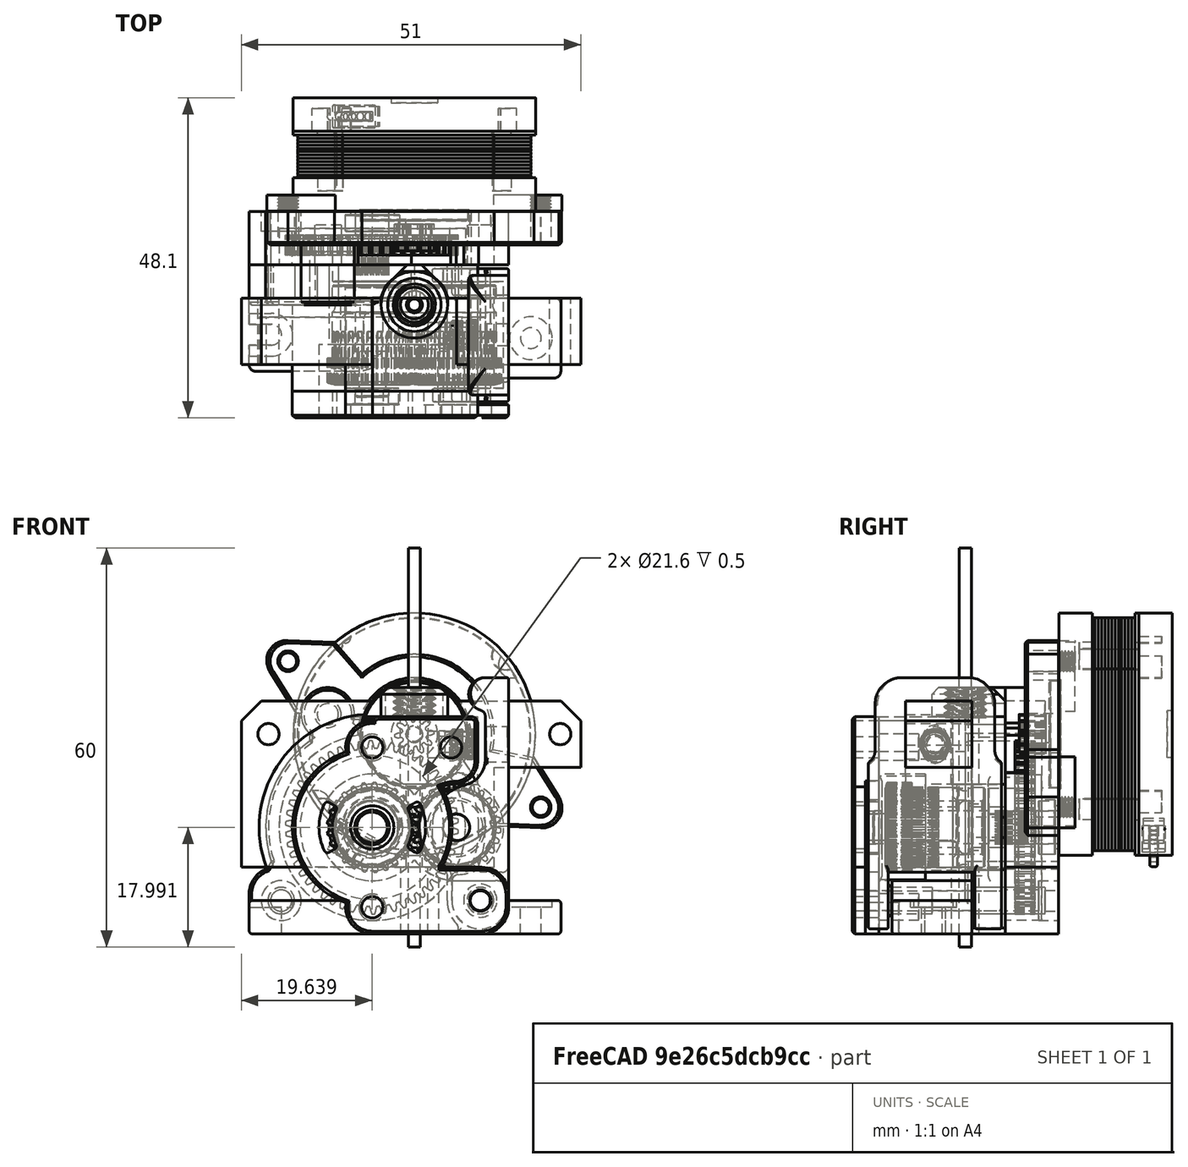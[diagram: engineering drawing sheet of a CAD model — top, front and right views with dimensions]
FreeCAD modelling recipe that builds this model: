
FCSTD DOCUMENT  (FreeCAD 0.18R16146 (Git))
Label: main-1
License: All rights reserved
LicenseURL: http://en.wikipedia.org/wiki/All_rights_reserved
objects: Part::Cylinder×61, Part::Cut×40, Part::MultiFuse×25, Part::Feature×21, Part::Box×20, Part::Fillet×20, Part::Chamfer×19, Part::MultiCommon×2
note: 208 computed .brp shape members not serialized (recipe doc carries the construction recipe); baked Part::Feature solids carry a one-line shape summary decoded from their .brp

FEATURE [Part::Feature] Part__Feature072  label="FlyGear"
  Placement = pos=(6.30321,-3.05009,17.9985) rot=(0,1,0;1.57818rad)
  shape: bbox 15.15 x 20 x 15.15 mm, 372 faces (baked)
FEATURE [Part::Feature] Part__Feature004  label="LatchShaft"
  Placement = pos=(9.90321,14.3499,6.99894) rot=(0.999993,0.00265,-0.00265;1.5708rad)
  shape: bbox 3.247 x 20 x 3.247 mm, 5 faces (baked)
FEATURE [Part::Feature] Part__Feature028  label="insert M3 v1"
  Placement = pos=(3.65321,4.45,30.4999) rot=(-0.57735,-0.57735,-0.57735;2.0944rad)
  shape: bbox 5.909 x 4.726 x 4.72 mm, 153 faces (baked)
FEATURE [Part::Feature] Part__Feature006  label="T10 SpurGear"
  Placement = pos=(3.9913e-08,-1.44113e-07,9e-15) rot=(0,0,1;0.017453rad)
  shape: bbox 6 x 5.817 x 5.76 mm, 83 faces (baked)
FEATURE [Part::Feature] Fusion001002002001003  label="name14"
  shape: bbox 50.3 x 39.95 x 23 mm, 596 faces (baked)
FEATURE [Part::MultiFuse] Fusion  label="moto-with-gear"
  Placement = pos=(0,17.1,32) rot=(-0.935113,0.250563,0.250563;1.63783rad)
  Shapes = -> [Part__Feature006,Fusion001002002001003]
FEATURE [Part::Feature] Fusion001  label="motor-cut"
  Placement = pos=(0,7e-15,32) rot=(-1,0,0;1.5708rad)
  shape: bbox 47.04 x 10 x 16.2 mm, 9 faces, 3 solids (baked)
FEATURE [Part::Box] Box  label="Cube"
  AttacherType = Attacher::AttachEngine3D
  Height = 25
  Length = 51
  Placement = pos=(-26,0,12) rot=(0,0,1;0rad)
  Width = 10
FEATURE [Part::Cylinder] Cylinder
  Angle = 360
  AttacherType = Attacher::AttachEngine3D
  Height = 10
  Placement = pos=(-6.325,-2.85,18) rot=(-1,0,0;1.5708rad)
  Radius = 17
FEATURE [Part::Cylinder] Cylinder001
  Angle = 360
  AttacherType = Attacher::AttachEngine3D
  Height = 10
  Placement = pos=(-6.325,8e-15,18) rot=(-1,0,0;1.5708rad)
  Radius = 3.25
FEATURE [Part::Cylinder] Cylinder002
  Angle = 360
  AttacherType = Attacher::AttachEngine3D
  Height = 10
  Placement = pos=(-6.325,-0.45,18) rot=(-1,0,0;1.5708rad)
  Radius = 4.1
FEATURE [Part::Cut] Cut
  Base = -> Box
  Tool = -> Cylinder
FEATURE [Part::Cut] Cut001
  Base = -> Cut
  Tool = -> Cylinder002
FEATURE [Part::Cut] Cut002
  Base = -> Cut001
  Tool = -> Cylinder001
FEATURE [Part::Chamfer] Chamfer
  Base = -> Cut002
  Edges = 1 edges r=0.5: [Edge25]
FEATURE [Part::Chamfer] Chamfer001
  Base = -> Chamfer
  Edges = 2 edges r=3: [Edge26,Edge27]
FEATURE [Part::Box] Box001  label="Cube001"
  AttacherType = Attacher::AttachEngine3D
  Height = 15
  Length = 14
  Placement = pos=(12,0,12) rot=(0,0,1;0rad)
  Width = 10
FEATURE [Part::Cut] Cut003
  Base = -> Chamfer001
  Tool = -> Box001
FEATURE [Part::Cut] Cut004  label="320-aligner-test"
  Base = -> Cut003
  Tool = -> Fusion001
FEATURE [Part::Feature] Common001001  label="back-plate-base"
  Placement = pos=(0,15,32) rot=(-0.935113,0.250563,0.250563;1.63783rad)
  shape: bbox 44.17 x 8 x 36 mm, 14 faces (baked)
FEATURE [Part::Cylinder] Cylinder003
  Angle = 360
  AttacherType = Attacher::AttachEngine3D
  Height = 8
  Placement = pos=(-6.325,23,18) rot=(1,0,0;1.5708rad)
  Radius = 16
FEATURE [Part::Feature] Part__Feature056001001002001  label="bearing002"
  shape: bbox 8 x 2.5 x 8 mm, 12 faces (baked)
FEATURE [Part::Feature] Fusion001001001  label="asembly-shaft001"
  Placement = pos=(0.2,0,0) rot=(0,0,1;0rad)
  shape: bbox 25.99 x 28 x 26 mm, 508 faces (baked)
FEATURE [Part::Feature] Part__Feature056001001001001  label="bearing003"
  Placement = pos=(0.2,0,0) rot=(0,0,1;0rad)
  shape: bbox 8 x 2.5 x 8 mm, 12 faces (baked)
FEATURE [Part::Feature] Part__Feature071001  label="MotorGear001"
  Placement = pos=(0.2,0,0) rot=(0,0,1;0rad)
  shape: bbox 14.64 x 15 x 14.64 mm, 359 faces (baked)
FEATURE [Part::Cylinder] Cylinder004
  Angle = 360
  AttacherType = Attacher::AttachEngine3D
  Height = 7
  Placement = pos=(-6.325,20.5,18) rot=(1,0,0;1.5708rad)
  Radius = 14
FEATURE [Part::Cylinder] Cylinder006
  Angle = 360
  AttacherType = Attacher::AttachEngine3D
  Height = 10
  Placement = pos=(-6.325,23,18) rot=(1,0,0;1.5708rad)
  Radius = 3.25
FEATURE [Part::Cylinder] Cylinder007
  Angle = 360
  AttacherType = Attacher::AttachEngine3D
  Height = 10
  Placement = pos=(-6.325,22.5,18) rot=(1,0,0;1.5708rad)
  Radius = 4.1
FEATURE [Part::Cylinder] Cylinder010  label="filament"
  Angle = 360
  AttacherType = Attacher::AttachEngine3D
  Height = 60
  Placement = pos=(0,9,0) rot=(0,0,1;0rad)
  Radius = 0.9
FEATURE [Part::Cylinder] Cylinder011
  Angle = 360
  AttacherType = Attacher::AttachEngine3D
  Height = 10
  Placement = pos=(0,18,32) rot=(1,0,0;1.5708rad)
  Radius = 27.1
FEATURE [Part::Cylinder] Cylinder012
  Angle = 142
  AttacherType = Attacher::AttachEngine3D
  Height = 10
  Placement = pos=(0,23,32) rot=(0.990855,0.095409,-0.095409;1.57998rad)
  Radius = 26
FEATURE [Part::Cylinder] Cylinder013
  Angle = 360
  AttacherType = Attacher::AttachEngine3D
  Height = 10
  Placement = pos=(0,23,32) rot=(1,0,0;1.5708rad)
  Radius = 12
FEATURE [Part::Feature] Fusion001002002001004  label="motor-cut001"
  Placement = pos=(0,23,32) rot=(0.935113,0.250563,-0.250563;1.63783rad)
  shape: bbox 41.07 x 10 x 25.02 mm, 9 faces, 3 solids (baked)
FEATURE [Part::Cut] Cut006
  Base = -> Cylinder012
  Tool = -> Cylinder013
FEATURE [Part::Cylinder] Cylinder014
  Angle = 360
  AttacherType = Attacher::AttachEngine3D
  Height = 10
  Placement = pos=(0,23,32) rot=(1,0,0;1.5708rad)
  Radius = 8.5
FEATURE [Part::Feature] Part__Feature  label="Latch"
  Placement = pos=(-6.34679,-10.5501,18) rot=(1,0,0;3.14159rad)
  shape: bbox 20.03 x 24 x 38.43 mm, 141 faces (baked)
FEATURE [Part::Cylinder] Cylinder015
  Angle = 360
  AttacherType = Attacher::AttachEngine3D
  Height = 10
  Placement = pos=(-6.325,22,18) rot=(1,0,0;1.5708rad)
  Radius = 15
FEATURE [Part::Chamfer] Chamfer008
  Base = -> Cylinder015
  Edges = 1 edges r=1: [Edge3]
FEATURE [Part::Box] Box002  label="Cube002"
  AttacherType = Attacher::AttachEngine3D
  Height = 10
  Length = 20.5
  Placement = pos=(-6.325,15,2) rot=(0,0,1;0rad)
  Width = 8
FEATURE [Part::Fillet] Fillet
  Base = -> Box002
  Edges = 1 edges r=5: [Edge8]
FEATURE [Part::Fillet] Fillet001
  Base = -> Fillet
  Edges = 1 edges r=4: [Edge3]
FEATURE [Part::Cylinder] Cylinder016
  Angle = 360
  AttacherType = Attacher::AttachEngine3D
  Height = 10
  Placement = pos=(9.925,21,7) rot=(1,0,0;1.5708rad)
  Radius = 2
FEATURE [Part::Box] Box003  label="Cube003"
  AttacherType = Attacher::AttachEngine3D
  Height = 10
  Length = 18.5
  Placement = pos=(-24.83,15,2) rot=(0,0,1;0rad)
  Width = 8
FEATURE [Part::Cylinder] Cylinder018  label="Cylinder017"
  Angle = 360
  AttacherType = Attacher::AttachEngine3D
  Height = 11
  Placement = pos=(-20,25,7) rot=(1,0,0;1.5708rad)
  Radius = 1.6
FEATURE [Part::Feature] Chamfer008001  label="Chamfer011"
  shape: bbox 30 x 10 x 30 mm, 4 faces (baked)
FEATURE [Part::Cylinder] Cylinder019  label="Cylinder018"
  Angle = 360
  AttacherType = Attacher::AttachEngine3D
  Height = 8
  Placement = pos=(-13,23,35) rot=(1,0,0;1.5708rad)
  Radius = 4
FEATURE [Part::Cylinder] Cylinder020  label="Cylinder019"
  Angle = 360
  AttacherType = Attacher::AttachEngine3D
  Height = 8
  Placement = pos=(-13,21,35) rot=(1,0,0;1.5708rad)
  Radius = 2
FEATURE [Part::Cut] Cut016
  Base = -> Common001001
  Tool = -> Cylinder011
FEATURE [Part::Cut] Cut017
  Base = -> Cut016
  Tool = -> Cut006
FEATURE [Part::Cut] Cut018
  Base = -> Cut017
  Tool = -> Fusion001002002001004
FEATURE [Part::Chamfer] Chamfer008002
  Base = -> Cut018
  Edges = 16 edges r=0.4: [Edge3,Edge24,Edge25,Edge26,Edge27,Edge28,Edge29,Edge30,Edge31,Edge32,Edge33,Edge34,Edge35,Edge36,Edge37,Edge39]
FEATURE [Part::Cylinder] Cylinder022
  Angle = 360
  AttacherType = Attacher::AttachEngine3D
  Height = 5
  Placement = pos=(-6.325,15,18) rot=(1,0,0;1.5708rad)
  Radius = 16
FEATURE [Part::Cylinder] Cylinder023
  Angle = 360
  AttacherType = Attacher::AttachEngine3D
  Height = 5
  Placement = pos=(6.325,15,18) rot=(1,0,0;1.5708rad)
  Radius = 6.5
FEATURE [Part::Cylinder] Cylinder024
  Angle = 360
  AttacherType = Attacher::AttachEngine3D
  Height = 5
  Placement = pos=(-6.325,15,18) rot=(1,0,0;1.5708rad)
  Radius = 6.5
FEATURE [Part::Box] Box008  label="Cube008"
  AttacherType = Attacher::AttachEngine3D
  Height = 10.65
  Length = 19.5
  Placement = pos=(-10,10,24) rot=(0,0,1;0rad)
  Width = 5
FEATURE [Part::Cylinder] Cylinder026
  Angle = 360
  AttacherType = Attacher::AttachEngine3D
  Height = 5
  Placement = pos=(-13,15,35) rot=(1,0,0;1.5708rad)
  Radius = 4
FEATURE [Part::Cylinder] Cylinder027
  Angle = 360
  AttacherType = Attacher::AttachEngine3D
  Height = 5
  Placement = pos=(-13,15,35) rot=(1,0,0;1.5708rad)
  Radius = 1.6
FEATURE [Part::Box] Box009  label="Cube009"
  AttacherType = Attacher::AttachEngine3D
  Height = 10
  Length = 32
  Placement = pos=(-24.83,10,2) rot=(0,0,1;0rad)
  Width = 5
FEATURE [Part::Cylinder] Cylinder028
  Angle = 360
  AttacherType = Attacher::AttachEngine3D
  Height = 5
  Placement = pos=(-20,15,7) rot=(1,0,0;1.5708rad)
  Radius = 2
FEATURE [Part::MultiFuse] Fusion001002002001008
  Shapes = -> [Cylinder028,Cylinder027]
FEATURE [Part::Box] Box010  label="Cube010"
  AttacherType = Attacher::AttachEngine3D
  Height = 12
  Length = 11
  Placement = pos=(4.925,10,7) rot=(0,0,1;0rad)
  Width = 5
FEATURE [Part::Box] Box011  label="Cube011"
  AttacherType = Attacher::AttachEngine3D
  Height = 13.5
  Length = 9
  Placement = pos=(6.325,10,11) rot=(0,0,1;0rad)
  Width = 5
FEATURE [Part::Cylinder] Cylinder029
  Angle = 360
  AttacherType = Attacher::AttachEngine3D
  Height = 5
  Placement = pos=(9.925,15,7) rot=(1,0,0;1.5708rad)
  Radius = 5
FEATURE [Part::Cut] Cut031002
  Base = -> Cylinder003
  Tool = -> Cylinder014
FEATURE [Part::Cut] Cut031004
  Base = -> Fillet001
  Tool = -> Chamfer008
FEATURE [Part::Cut] Cut031005
  Base = -> Cut031004
  Tool = -> Cylinder016
FEATURE [Part::Chamfer] Chamfer008007
  Base = -> Cut031002
  Edges = 2 edges r=1: [Edge3,Edge6]
FEATURE [Part::Cylinder] Cylinder030
  Angle = 360
  AttacherType = Attacher::AttachEngine3D
  Height = 1
  Placement = pos=(-20,10,7) rot=(1,0,0;1.5708rad)
  Radius = 3
FEATURE [Part::Cylinder] Cylinder031
  Angle = 360
  AttacherType = Attacher::AttachEngine3D
  Height = 15
  Placement = pos=(-6.325,11,18) rot=(1,0,0;1.5708rad)
  Radius = 6.5
FEATURE [Part::Cylinder] Cylinder032
  Angle = 360
  AttacherType = Attacher::AttachEngine3D
  Height = 14
  Placement = pos=(-6.325,10,18) rot=(1,0,0;1.5708rad)
  Radius = 12
FEATURE [Part::Cylinder] Cylinder033
  Angle = 360
  AttacherType = Attacher::AttachEngine3D
  Height = 15
  Placement = pos=(-6.325,3,18) rot=(1,0,0;1.5708rad)
  Radius = 8
FEATURE [Part::Cylinder] Cylinder034
  Angle = 360
  AttacherType = Attacher::AttachEngine3D
  Height = 14
  Placement = pos=(-6.325,10,6) rot=(1,0,0;1.5708rad)
  Radius = 4
FEATURE [Part::Cylinder] Cylinder035
  Angle = 360
  AttacherType = Attacher::AttachEngine3D
  Height = 14
  Placement = pos=(-6.325,10,30) rot=(1,0,0;1.5708rad)
  Radius = 4
FEATURE [Part::Cylinder] Cylinder036
  Angle = 360
  AttacherType = Attacher::AttachEngine3D
  Height = 6
  Placement = pos=(-6.325,2,6) rot=(1,0,0;1.5708rad)
  Radius = 2
FEATURE [Part::Cylinder] Cylinder037
  Angle = 360
  AttacherType = Attacher::AttachEngine3D
  Height = 6
  Placement = pos=(-6.325,2,30) rot=(1,0,0;1.5708rad)
  Radius = 2
FEATURE [Part::Box] Box013  label="Cube013"
  AttacherType = Attacher::AttachEngine3D
  Height = 36
  Length = 20
  Placement = pos=(-6.325,-13,0) rot=(0,0,1;0rad)
  Width = 10
FEATURE [Part::Box] Box014  label="Cube014"
  AttacherType = Attacher::AttachEngine3D
  Height = 5
  Length = 22
  Placement = pos=(0,-2,2) rot=(0,0,1;0rad)
  Width = 12
FEATURE [Part::Box] Box015  label="Cube015"
  AttacherType = Attacher::AttachEngine3D
  Height = 5
  Length = 22
  Placement = pos=(-24.83,-1,2) rot=(0,0,1;0rad)
  Width = 11
FEATURE [Part::Box] Box016  label="Cube016"
  AttacherType = Attacher::AttachEngine3D
  Height = 8
  Length = 9.5
  Placement = pos=(4.675,-2,2) rot=(0,0,1;0rad)
  Width = 12
FEATURE [Part::Fillet] Fillet007
  Base = -> Box016
  Edges = 1 edges r=2: [Edge6]
FEATURE [Part::Fillet] Fillet008
  Base = -> Box003
  Edges = 1 edges r=4: [Edge2]
FEATURE [Part::Fillet] Fillet009
  Base = -> Fillet008
  Edges = 1 edges r=0.5: [Edge3]
FEATURE [Part::Cut] Cut031012
  Base = -> Fillet009
  Tool = -> Chamfer008001
FEATURE [Part::MultiFuse] Fusion001002002001013
  Shapes = -> [Cut031012,Chamfer008007,Cylinder019,Cut031005,Chamfer008002]
FEATURE [Part::Cut] Cut031013
  Base = -> Fusion001002002001013
  Tool = -> Cylinder004
FEATURE [Part::Cut] Cut031014
  Base = -> Cut031013
  Tool = -> Cylinder007
FEATURE [Part::Cut] Cut031015
  Base = -> Cut031014
  Tool = -> Cylinder006
FEATURE [Part::MultiFuse] Fusion001002002001014
  Shapes = -> [Cylinder020,Cylinder018]
FEATURE [Part::Fillet] Fillet010
  Base = -> Box009
  Edges = 1 edges r=4: [Edge2]
FEATURE [Part::Fillet] Fillet011
  Base = -> Fillet010
  Edges = 1 edges r=0.5: [Edge3]
FEATURE [Part::MultiFuse] Fusion001002002001015
  Shapes = -> [Fillet011,Cylinder022,Cylinder026,Box008]
FEATURE [Part::Chamfer] Chamfer008005003003004
  Base = -> Cut031015
  Edges = 2 edges r=1: [Edge6,Edge40]
FEATURE [Part::MultiFuse] Fusion001002002001016
  Shapes = -> [Cylinder023,Cylinder024]
FEATURE [Part::Cut] Cut031025
  Base = -> Fusion001002002001015
  Tool = -> Fusion001002002001016
FEATURE [Part::Cut] Cut031026
  Base = -> Cut031025
  Tool = -> Fusion001002002001008
FEATURE [Part::Chamfer] Chamfer008005003003005
  Base = -> Cut031026
  Edges = 1 edges r=1: [Edge15]
FEATURE [Part::MultiFuse] Fusion001002002001017
  Shapes = -> [Box011,Box010,Cylinder029]
FEATURE [Part::Cut] Cut031027  label="mid-base-draf"
  Base = -> Chamfer008005003003005
  Tool = -> Fusion001002002001017
FEATURE [Part::Feature] Cut031027001  label="mid-base-draf001"
  shape: bbox 34.33 x 5 x 37 mm, 19 faces (baked)
FEATURE [Part::Fillet] Fillet012
  Base = -> Cut031027001
  Edges = 1 edges r=3.5: [Edge35]
FEATURE [Part::Fillet] Fillet013
  Base = -> Fillet012
  Edges = 5 edges r=1: [Edge5,Edge58,Edge59,Edge64,Edge69]
FEATURE [Part::Chamfer] Chamfer008005003003006  label="mid-plate-base"
  Base = -> Fillet013
  Edges = 2 edges r=1: [Edge73,Edge76]
FEATURE [Part::Feature] Chamfer008005003003006001  label="mid-plate-base002"
  Placement = pos=(0,-20,0) rot=(0,0,1;0rad)
  shape: bbox 34.33 x 5.612 x 37 mm, 26 faces (baked)
FEATURE [Part::Feature] Chamfer008005003003006002  label="mid-plate-base003"
  Placement = pos=(0,-1,0) rot=(0,0,1;0rad)
  shape: bbox 34.33 x 5.612 x 37 mm, 26 faces (baked)
FEATURE [Part::Chamfer] Chamfer008005003003006003
  Base = -> Chamfer008005003003006002
  Edges = 30 edges r=0.4: [Edge1,Edge2,Edge3,Edge4,Edge5,Edge6,Edge7,Edge8,Edge9,Edge10,Edge11,Edge12,Edge13,Edge14,Edge15,Edge16,Edge17,Edge18,Edge19,Edge20,Edge21,Edge22,Edge23,Edge24,Edge25,Edge26,Edge27,Edge28,Edge29,Edge30]
FEATURE [Part::MultiFuse] Fusion001002002001018  label="mid-plate-chamfer-adt"
  Shapes = -> [Chamfer008005003003006003,Cylinder030]
FEATURE [Part::Cylinder] Cylinder039
  Angle = 360
  AttacherType = Attacher::AttachEngine3D
  Height = 1
  Placement = pos=(17.5,4,6) rot=(0,0,1;0rad)
  Radius = 3.2
FEATURE [Part::Cylinder] Cylinder040
  Angle = 360
  AttacherType = Attacher::AttachEngine3D
  Height = 10
  Placement = pos=(-21.5,4.5,0) rot=(0,0,1;0rad)
  Radius = 1.55
FEATURE [Part::Fillet] Fillet016
  Base = -> Box014
  Edges = 2 edges r=1: [Edge5,Edge7]
FEATURE [Part::Fillet] Fillet017
  Base = -> Fillet016
  Edges = 10 edges r=0.4: [Edge1,Edge4,Edge5,Edge6,Edge8,Edge9,Edge10,Edge12,Edge14,Edge16]
FEATURE [Part::Fillet] Fillet018
  Base = -> Fillet007
  Edges = 2 edges r=0.4: [Edge6,Edge12]
FEATURE [Part::Cylinder] Cylinder041
  Angle = 360
  AttacherType = Attacher::AttachEngine3D
  Height = 30
  Placement = pos=(17.5,4,0) rot=(0,0,1;0rad)
  Radius = 1.55
FEATURE [Part::Cut] Cut031027003
  Base = -> Fillet017
  Tool = -> Cylinder041
FEATURE [Part::Cut] Cut031027004
  Base = -> Cut031027003
  Tool = -> Cylinder039
FEATURE [Part::Box] Box017  label="Cube017"
  AttacherType = Attacher::AttachEngine3D
  Height = 10
  Length = 6.5
  Placement = pos=(-28,2.95,0) rot=(0,0,1;0rad)
  Width = 3.1
FEATURE [Part::Cylinder] Cylinder042
  Angle = 360
  AttacherType = Attacher::AttachEngine3D
  Height = 1
  Placement = pos=(-21.5,4.5,0) rot=(0,0,1;0rad)
  Radius = 3.2
FEATURE [Part::Box] Box018  label="Cube018"
  AttacherType = Attacher::AttachEngine3D
  Height = 1
  Length = 6.5
  Placement = pos=(-28,1.3,0) rot=(0,0,1;0rad)
  Width = 6.4
FEATURE [Part::MultiFuse] Fusion001002002001022
  Shapes = -> [Cylinder040,Box017]
FEATURE [Part::MultiFuse] Fusion001002002001023
  Placement = pos=(0,0,6) rot=(0,0,1;0rad)
  Shapes = -> [Cylinder042,Box018]
FEATURE [Part::MultiCommon] Common
  Placement = pos=(0,15,0) rot=(0,0,1;0rad)
  Shapes = -> [Chamfer008005003003006001,Box013]
FEATURE [Part::Fillet] Fillet019
  Base = -> Common
  Edges = 1 edges r=1: [Edge13]
FEATURE [Part::Feature] Fillet019001  label="Fillet020"
  Placement = pos=(0,-4,0) rot=(0,0,1;0rad)
  shape: bbox 15.83 x 5.612 x 32.65 mm, 23 faces, 2 solids (baked)
FEATURE [Part::Feature] Fillet019002  label="Fillet021"
  Placement = pos=(0,-9,0) rot=(0,0,1;0rad)
  shape: bbox 15.83 x 5.612 x 32.65 mm, 23 faces, 2 solids (baked)
FEATURE [Part::Cylinder] Cylinder043
  Angle = 360
  AttacherType = Attacher::AttachEngine3D
  Height = 15
  Placement = pos=(9.925,11,7) rot=(1,0,0;1.5708rad)
  Radius = 1.5
FEATURE [Part::Cylinder] Cylinder044  label="filament-path"
  Angle = 360
  AttacherType = Attacher::AttachEngine3D
  Height = 60
  Placement = pos=(0,9,0) rot=(0,0,1;0rad)
  Radius = 1.2
FEATURE [Part::Cylinder] Cylinder045  label="Cylinder044"
  Angle = 360
  AttacherType = Attacher::AttachEngine3D
  Height = 12
  Placement = pos=(2,4.4,30.5) rot=(0,1,0;1.5708rad)
  Radius = 2
FEATURE [Part::Cylinder] Cylinder046  label="Cylinder045"
  Angle = 360
  AttacherType = Attacher::AttachEngine3D
  Height = 6
  Placement = pos=(5.5,2,30) rot=(1,0,0;1.5708rad)
  Radius = 2
FEATURE [Part::Fillet] Fillet019003
  Base = -> Box015
  Edges = 1 edges r=1: [Edge1]
FEATURE [Part::Fillet] Fillet019004
  Base = -> Fillet019003
  Edges = 6 edges r=0.5: [Edge1,Edge4,Edge5,Edge7,Edge9,Edge13]
FEATURE [Part::Cut] Cut031027011002002
  Base = -> Fillet019004
  Tool = -> Fusion001002002001022
FEATURE [Part::Cut] Cut031027011002003
  Base = -> Cut031027011002002
  Tool = -> Fusion001002002001023
FEATURE [Part::MultiFuse] Fusion001002002001019004
  Shapes = -> [Chamfer008005003003006,Fusion001002002001018]
FEATURE [Part::MultiFuse] Fusion001002002001019005
  Shapes = -> [Fillet019,Fillet019001,Fillet019002]
FEATURE [Part::Cylinder] Cylinder047
  Angle = 360
  AttacherType = Attacher::AttachEngine3D
  Height = 15
  Placement = pos=(6.325,11,18) rot=(1,0,0;1.5708rad)
  Radius = 6.5
FEATURE [Part::Cylinder] Cylinder048
  Angle = 360
  AttacherType = Attacher::AttachEngine3D
  Height = 15
  Placement = pos=(6.325,3,18) rot=(1,0,0;1.5708rad)
  Radius = 8
FEATURE [Part::MultiFuse] Fusion001002002001019006
  Shapes = -> [Cylinder031,Cylinder033]
FEATURE [Part::MultiFuse] Fusion001002002001019007
  Shapes = -> [Cylinder048,Cylinder047]
FEATURE [Part::MultiFuse] Fusion001002002001019008
  Shapes = -> [Fusion001002002001019006,Fusion001002002001019007]
FEATURE [Part::MultiFuse] Fusion001002002001019009
  Shapes = -> [Cylinder032,Cut031027011002003,Fillet018,Cut031027004,Cylinder035,Cylinder034,Fusion001002002001019004,Fusion001002002001019005]
FEATURE [Part::Cut] Cut031027011002004
  Base = -> Fusion001002002001019009
  Tool = -> Fusion001002002001019008
FEATURE [Part::Fillet] Fillet019005
  Base = -> Cut031027011002004
  Edges = 2 edges r=1: [Edge11,Edge39]
FEATURE [Part::Cylinder] Cylinder049
  Angle = 360
  AttacherType = Attacher::AttachEngine3D
  Height = 6
  Placement = pos=(9.925,4,7) rot=(1,0,0;1.5708rad)
  Radius = 2
FEATURE [Part::MultiFuse] Fusion001002002001019010
  Shapes = -> [Cylinder049,Cylinder036,Cylinder037,Cylinder043]
FEATURE [Part::Cut] Cut031027011002005
  Base = -> Fillet019005
  Tool = -> Fusion001002002001019010
FEATURE [Part::Cut] Cut031027011002006
  Base = -> Cut031027011002005
  Tool = -> Cylinder044
FEATURE [Part::MultiFuse] Fusion001002002001019011
  Shapes = -> [Cylinder046,Cylinder045]
FEATURE [Part::Cut] Cut031027011002007
  Base = -> Cut031027011002006
  Tool = -> Fusion001002002001019011
FEATURE [Part::Cylinder] Cylinder050
  Angle = 360
  AttacherType = Attacher::AttachEngine3D
  Height = 12
  Placement = pos=(0,9,0) rot=(0,0,1;0rad)
  Radius = 2.05
FEATURE [Part::Cut] Cut031027011002009
  Base = -> Chamfer008005003003004
  Tool = -> Fusion001002002001014
FEATURE [Part::Cylinder] Cylinder051
  Angle = 360
  AttacherType = Attacher::AttachEngine3D
  Height = 10
  Placement = pos=(9.925,16,7) rot=(1,0,0;4.71239rad)
  Radius = 1.55
FEATURE [Part::Cylinder] Cylinder052
  Angle = 360
  AttacherType = Attacher::AttachEngine3D
  Height = 3
  Placement = pos=(-20,20,7) rot=(1,0,0;4.71239rad)
  Radius = 3
FEATURE [Part::Cut] Cut031027011002010
  Base = -> Cut031027011002009
  Tool = -> Cylinder052
FEATURE [Part::Cut] Cut031027011002011  label="back-t3"
  Base = -> Cut031027011002010
  Tool = -> Cylinder051
FEATURE [Part::Cylinder] Cylinder053
  Angle = 360
  AttacherType = Attacher::AttachEngine3D
  Height = 2
  Placement = pos=(-6.325,-4,18) rot=(1,0,0;1.5708rad)
  Radius = 4.1
FEATURE [Part::Cylinder] Cylinder054
  Angle = 360
  AttacherType = Attacher::AttachEngine3D
  Height = 8
  Placement = pos=(-6.325,-4,18) rot=(1,0,0;1.5708rad)
  Radius = 3.25
FEATURE [Part::Cylinder] Cylinder055
  Angle = 360
  AttacherType = Attacher::AttachEngine3D
  Height = 4
  Placement = pos=(-6.325,-4,6) rot=(1,0,0;1.5708rad)
  Radius = 4
FEATURE [Part::Cylinder] Cylinder056
  Angle = 360
  AttacherType = Attacher::AttachEngine3D
  Height = 4
  Placement = pos=(-6.325,-4,30) rot=(1,0,0;1.5708rad)
  Radius = 4
FEATURE [Part::Cylinder] Cylinder057
  Angle = 360
  AttacherType = Attacher::AttachEngine3D
  Height = 4
  Placement = pos=(-6.325,-4,18) rot=(1,0,0;1.5708rad)
  Radius = 12
FEATURE [Part::Feature] Fusion001002002001019005001  label="Fusion001002002001019012"
  Placement = pos=(0,-14,0) rot=(0,0,1;0rad)
  shape: bbox 15.83 x 14.61 x 32.65 mm, 80 faces, 2 solids (baked)
FEATURE [Part::Box] Box019  label="Cube019"
  AttacherType = Attacher::AttachEngine3D
  Height = 38
  Length = 24
  Placement = pos=(-9,-8,0) rot=(0,0,1;0rad)
  Width = 4
FEATURE [Part::MultiCommon] Common001002
  Shapes = -> [Box019,Fusion001002002001019005001]
FEATURE [Part::Box] Box020  label="Cube020"
  AttacherType = Attacher::AttachEngine3D
  Height = 10
  Length = 11
  Placement = pos=(3.15,-8,2) rot=(0,0,1;0rad)
  Width = 2
FEATURE [Part::Fillet] Fillet019006
  Base = -> Box020
  Edges = 1 edges r=4: [Edge8]
FEATURE [Part::Fillet] Fillet019007
  Base = -> Fillet019006
  Edges = 1 edges r=4: [Edge3]
FEATURE [Part::Cylinder] Cylinder058
  Angle = 360
  AttacherType = Attacher::AttachEngine3D
  Height = 10
  Placement = pos=(9.925,0,7) rot=(1,0,0;1.5708rad)
  Radius = 1.6
FEATURE [Part::Cut] Cut031027011002012
  Base = -> Fillet019007
  Tool = -> Cylinder058
FEATURE [Part::MultiFuse] Fusion001002002001019005003
  Shapes = -> [Cylinder054,Cylinder053]
FEATURE [Part::Box] Box021  label="Cube021"
  AttacherType = Attacher::AttachEngine3D
  Height = 14.5
  Length = 10
  Placement = pos=(1.425,-6,10.5) rot=(0,0,1;0rad)
  Width = 10
FEATURE [Part::Fillet] Fillet019008
  Base = -> Box021
  Edges = 2 edges r=5: [Edge2,Edge4]
FEATURE [Part::Cylinder] Cylinder059
  Angle = 360
  AttacherType = Attacher::AttachEngine3D
  Height = 10
  Placement = pos=(-6.325,1.3e-15,6) rot=(1,0,0;1.5708rad)
  Radius = 1.6
FEATURE [Part::Cylinder] Cylinder060
  Angle = 360
  AttacherType = Attacher::AttachEngine3D
  Height = 10
  Placement = pos=(-6.325,6.3e-15,30) rot=(1,0,0;1.5708rad)
  Radius = 1.6
FEATURE [Part::Chamfer] Chamfer008005003003006004
  Base = -> Cylinder057
  Edges = 1 edges r=0.4: [Edge1]
FEATURE [Part::Chamfer] Chamfer008005003003006005
  Base = -> Cylinder056
  Edges = 1 edges r=0.4: [Edge1]
FEATURE [Part::Chamfer] Chamfer008005003003006006
  Base = -> Cylinder055
  Edges = 1 edges r=0.4: [Edge1]
FEATURE [Part::Box] Box022  label="Cube022"
  AttacherType = Attacher::AttachEngine3D
  Height = 19
  Length = 24
  Placement = pos=(-9,-8,0) rot=(0,0,1;0rad)
  Width = 4
FEATURE [Part::Cut] Cut031027011002013
  Base = -> Common001002
  Tool = -> Box022
FEATURE [Part::Chamfer] Chamfer008005003003006007
  Base = -> Cut031027011002013
  Edges = 11 edges r=0.4: [Edge1,Edge2,Edge3,Edge4,Edge5,Edge6,Edge7,Edge8,Edge9,Edge10,Edge11]
FEATURE [Part::Box] Box023  label="Cube023"
  AttacherType = Attacher::AttachEngine3D
  Height = 10
  Length = 10
  Placement = pos=(-6.325,-8,2) rot=(0,0,1;0rad)
  Width = 4
FEATURE [Part::Chamfer] Chamfer008005003003006009
  Base = -> Cut031027011002012
  Edges = 5 edges r=0.4: [Edge1,Edge5,Edge6,Edge7,Edge8]
FEATURE [Part::Cylinder] Cylinder061
  Angle = 360
  AttacherType = Attacher::AttachEngine3D
  Height = 10
  Placement = pos=(5.5,6.7e-15,30) rot=(1,0,0;1.5708rad)
  Radius = 1.6
FEATURE [Part::MultiFuse] Fusion001002002001019005006
  Shapes = -> [Cylinder059,Cylinder060,Cylinder061]
FEATURE [Part::Cylinder] Cylinder062
  Angle = 60
  AttacherType = Attacher::AttachEngine3D
  Height = 11
  Placement = pos=(-6.325,4e-15,18) rot=(-0.935113,-0.250563,0.250563;4.64535rad)
  Radius = 6
FEATURE [Part::Cylinder] Cylinder063
  Angle = 60
  AttacherType = Attacher::AttachEngine3D
  Height = 11
  Placement = pos=(-6.325,4e-15,18) rot=(0.186157,-0.694747,0.694747;2.77349rad)
  Radius = 6
FEATURE [Part::Cylinder] Cylinder064
  Angle = 60
  AttacherType = Attacher::AttachEngine3D
  Height = 11
  Placement = pos=(-6.325,4e-15,18) rot=(0.186157,-0.694747,0.694747;2.77349rad)
  Radius = 8
FEATURE [Part::Cylinder] Cylinder065
  Angle = 60
  AttacherType = Attacher::AttachEngine3D
  Height = 11
  Placement = pos=(-6.325,4e-15,18) rot=(0.935113,0.250563,-0.250563;1.63783rad)
  Radius = 8
FEATURE [Part::MultiFuse] Fusion001002002001019005007
  Shapes = -> [Cylinder063,Cylinder062]
FEATURE [Part::MultiFuse] Fusion001002002001019005008
  Shapes = -> [Cylinder065,Cylinder064]
FEATURE [Part::Cut] Cut031027011002017
  Base = -> Fusion001002002001019005008
  Tool = -> Fusion001002002001019005007
FEATURE [Part::Fillet] Fillet019009
  Base = -> Cut031027011002017
  Edges = 8 edges r=0.5: [Edge2,Edge4,Edge9,Edge12,Edge13,Edge15,Edge18,Edge22]
FEATURE [Part::Feature] Cut001_solid  label="m6-thread"
  Placement = pos=(0,9,34.5) rot=(0,0,1;0rad)
  shape: bbox 7.534 x 7.534 x 10.4 mm, 26 faces (baked)
FEATURE [Part::Cylinder] Cylinder066
  Angle = 360
  AttacherType = Attacher::AttachEngine3D
  Height = 4.5
  Placement = pos=(0,9,34.5) rot=(0,0,1;0rad)
  Radius = 5
FEATURE [Part::Box] Box024  label="Cube024"
  AttacherType = Attacher::AttachEngine3D
  Height = 3.5
  Length = 10
  Placement = pos=(-5,9,34.5) rot=(0,0,1;0rad)
  Width = 6
FEATURE [Part::Chamfer] Chamfer008005003003006012
  Base = -> Cylinder066
  Edges = 1 edges r=1: [Edge1]
FEATURE [Part::Chamfer] Chamfer008005003003006013
  Base = -> Box024
  Edges = 2 edges r=3.9: [Edge3,Edge7]
FEATURE [Part::Chamfer] Chamfer008005003003006014
  Base = -> Chamfer008005003003006013
  Edges = 2 edges r=1: [Edge2,Edge18]
FEATURE [Part::Chamfer] Chamfer008005003003006015
  Base = -> Chamfer008005003003006014
  Edges = 1 edges r=1: [Edge9]
FEATURE [Part::MultiFuse] Fusion001002002001019005009
  Shapes = -> [Chamfer008005003003006015,Chamfer008005003003006012]
FEATURE [Part::Cylinder] Cylinder067  label="ptfe-path"
  Angle = 360
  AttacherType = Attacher::AttachEngine3D
  Height = 60
  Placement = pos=(0,9,24.5) rot=(0,0,1;0rad)
  Radius = 2.1
FEATURE [Part::Cut] Cut031027011002019
  Base = -> Cut031027011002007
  Tool = -> Cylinder050
FEATURE [Part::MultiFuse] Fusion001002002001019005010
  Shapes = -> [Fusion001002002001019005009,Cut031027011002019]
FEATURE [Part::Cut] Cut031027011002020
  Base = -> Fusion001002002001019005010
  Tool = -> Cylinder067
FEATURE [Part::Cut] Cut031027011002021  label="mid-t2"
  Base = -> Cut031027011002020
  Tool = -> Cut001_solid
FEATURE [Part::Chamfer] Chamfer008005003003006016
  Base = -> Box023
  Edges = 1 edges r=0.4: [Edge9]
FEATURE [Part::MultiFuse] Fusion001002002001019005011
  Shapes = -> [Chamfer008005003003006016,Chamfer008005003003006004,Chamfer008005003003006005,Chamfer008005003003006006,Chamfer008005003003006007,Chamfer008005003003006009]
FEATURE [Part::Cut] Cut031027011002021002
  Base = -> Fusion001002002001019005011
  Tool = -> Fillet019008
FEATURE [Part::Cut] Cut031027011002021003
  Base = -> Cut031027011002021002
  Tool = -> Fusion001002002001019005006
FEATURE [Part::Cut] Cut031027011002021004
  Base = -> Cut031027011002021003
  Tool = -> Fusion001002002001019005003
FEATURE [Part::Cut] Cut031027011002021005  label="front-t1"
  Base = -> Cut031027011002021004
  Tool = -> Fillet019009
